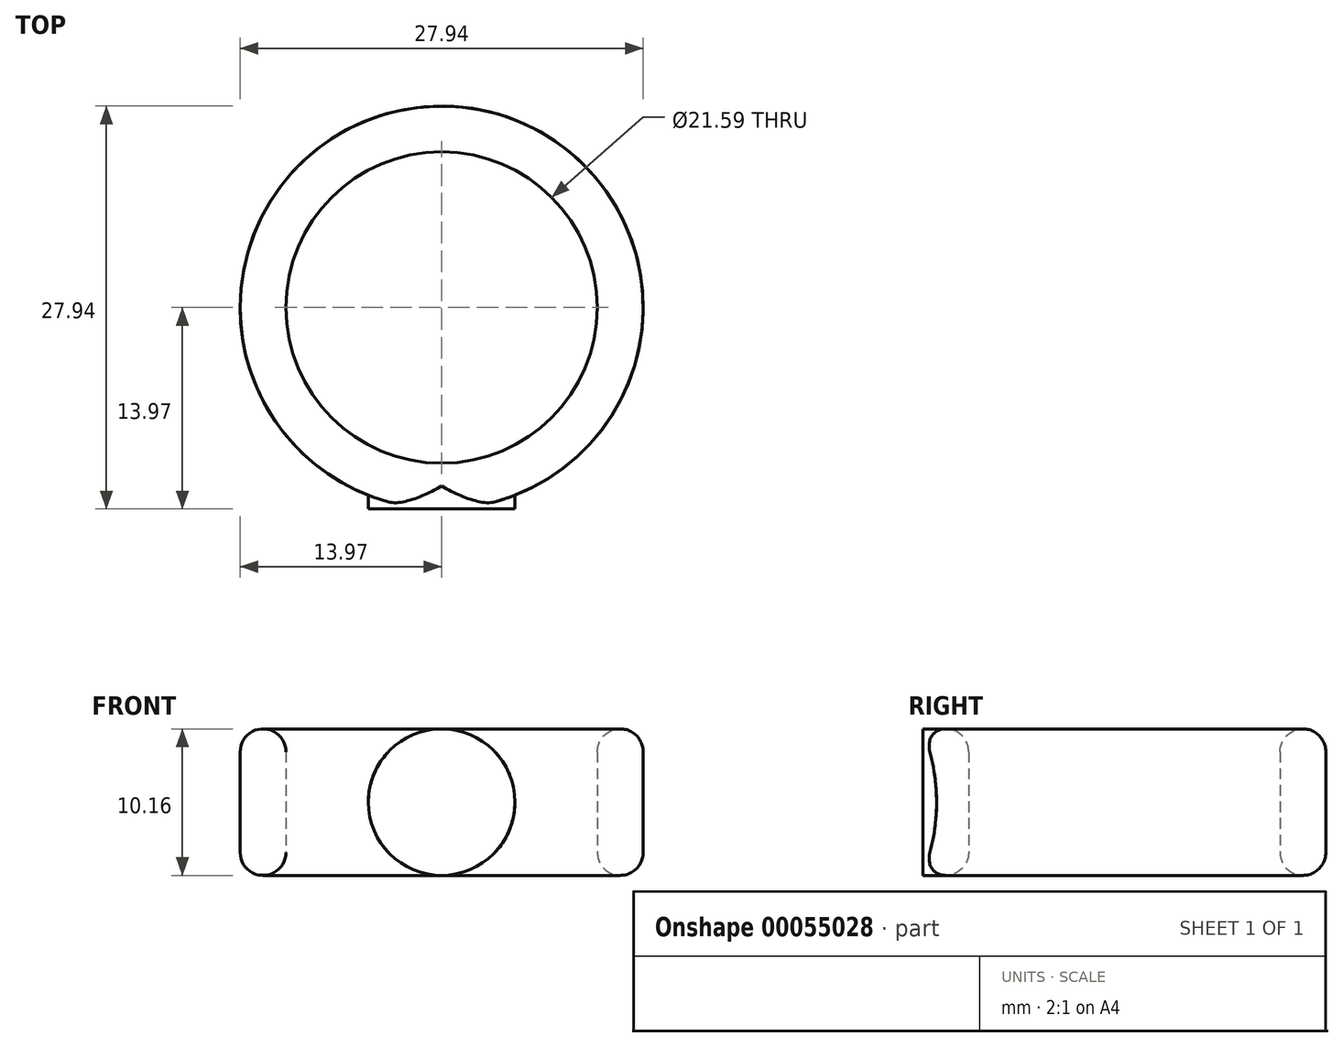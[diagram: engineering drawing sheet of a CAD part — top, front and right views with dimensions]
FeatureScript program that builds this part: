
annotation { "Feature Type Name" : "Feature", "Feature Type Description" : "" }
export const myFeature = defineFeature(function(context is Context, id is Id, definition is map)
    precondition{}
    {
        {
            var Q0;
            Q0=qCreatedBy(makeId("Front.planeOp"),FACE);
            var sketch = newSketch(context, id + "F0", { "sketchPlane" : qUnion([Q0])});
            skLineSegment(sketch, "E0", {"start": v(0, 0) * mm, "end": v(0, 29.6) * mm});
            skLineSegment(sketch, "E1", {"start": v(10.8, -0.35) * mm, "end": v(10.8, -7.34) * mm});
            skLineSegment(sketch, "E2", {"start": v(12.38, -8.93) * mm, "end": v(12.38, -8.93) * mm});
            skLineSegment(sketch, "E3", {"start": v(13.97, -7.34) * mm, "end": v(13.97, -0.35) * mm});
            skLineSegment(sketch, "E4", {"start": v(12.38, 1.23) * mm, "end": v(12.38, 1.23) * mm});
            skPoint(sketch, "E5.visualSharp", {"position": v(10.8, 1.23) * mm});
            skArc(sketch, "E5.filletArc", {"start": v(12.38, 1.23) * mm, "mid": v(11.26, 0.77) * mm, "end": v(10.8, -0.35) * mm});
            skPoint(sketch, "E6.visualSharp", {"position": v(13.97, 1.23) * mm});
            skArc(sketch, "E6.filletArc", {"start": v(13.97, -0.35) * mm, "mid": v(13.5, 0.77) * mm, "end": v(12.38, 1.23) * mm});
            skPoint(sketch, "E7.visualSharp", {"position": v(10.8, -8.93) * mm});
            skArc(sketch, "E7.filletArc", {"start": v(10.8, -7.34) * mm, "mid": v(11.26, -8.46) * mm, "end": v(12.38, -8.93) * mm});
            skPoint(sketch, "E8.visualSharp", {"position": v(13.97, -8.93) * mm});
            skArc(sketch, "E8.filletArc", {"start": v(12.38, -8.93) * mm, "mid": v(13.5, -8.46) * mm, "end": v(13.97, -7.34) * mm});
            skLineSegment(sketch, "E9", {"start": v(12.38, 1.23) * mm, "end": v(7.96, 1.23) * mm});
            skLineSegment(sketch, "E10", {"start": v(7.96, 1.23) * mm, "end": v(7.96, -8.93) * mm});
            skLineSegment(sketch, "E11", {"start": v(7.96, -8.93) * mm, "end": v(12.38, -8.93) * mm});
            skSolve(sketch);
        }
        {
            var Q0;
            Q0=makeQuery(id+"F0.imprint","IMPRINT",FACE,{"disambiguationData":[TD([[makeQuery(id+"F0.imprint","IMPRINT",EDGE,{"derivedFrom":sQuery(id+"F0.wireOp",EDGE,"E1")}),1.0]])]});
            var Q1;
            Q1=sQuery(id+"F0.wireOp",EDGE,"E0");
            revolve(context, id + "F1", {"entities" : qUnion([Q0]), "axis" : qUnion([Q1]), "revolveType" : RevolveType.FULL});
        }
        {
            var Q0;
            Q0=qCreatedBy(makeId("Front.planeOp"),FACE);
            cPlane(context, id + "F2", {"entities" : qUnion([Q0]), "cplaneType" : CPlaneType.OFFSET, "offset" : 10.8 * mm, "width" : 152.4 * mm, "height" : 152.4 * mm});
        }
        {
            var Q0;
            Q0=qCreatedBy(id+"F2.planeOp",FACE);
            var sketch = newSketch(context, id + "F3", { "sketchPlane" : qUnion([Q0])});
            skCircle(sketch, "E12", {"center": v(0, -3.85) * mm, "radius": 5.08 * mm});
            skSolve(sketch);
        }
        {
            var Q0;
            Q0 = qSketchRegion(id + "F3", true);
            extrude(context, id + "F4", {"entities" : qUnion([Q0]), "operationType" : NewBodyOperationType.ADD, "depth" : 3.17 * mm});
        }
        {
            var Q0;
            Q0=makeQuery(id+"F0.imprint","IMPRINT",FACE,{"disambiguationData":[TD([[makeQuery(id+"F0.imprint","IMPRINT",EDGE,{"derivedFrom":sQuery(id+"F0.wireOp",EDGE,"E1")}),-1.0]])]});
            var Q1;
            Q1=sQuery(id+"F0.wireOp",EDGE,"E0");
            revolve(context, id + "F5", {"operationType" : NewBodyOperationType.REMOVE, "entities" : qUnion([Q0]), "axis" : qUnion([Q1]), "revolveType" : RevolveType.FULL, "oppositeDirection" : true});
        }
    });
